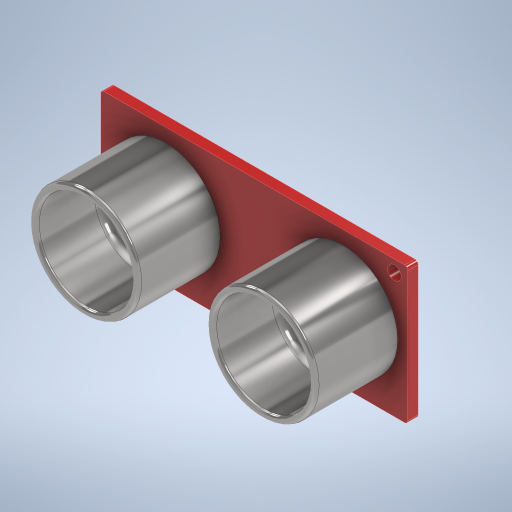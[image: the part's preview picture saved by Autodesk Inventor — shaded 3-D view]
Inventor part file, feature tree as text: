
AUTODESK INVENTOR PART (.ipt)
format: ipt  version: 2023 (Build 270158000, 158)  size: 452,608 bytes
history: native  units: mm
features: extrude x5, fillet x5, other x4, sketch x3, projected_geometry x2, mirror x1
ambient origin geometry x8: Origin, YZ Plane, XZ Plane, XY Plane, X Axis, Y Axis, Z Axis, Center Point
bodies: Body1 (feature_tree), Body2 (feature_tree), Body3 (feature_tree), Body4 (feature_tree)
feature tree (20):
  other  "Sólido1"
  sketch  "Boceto1"  dims[d0=45.0mm d1=20.0mm]
  extrude  "Extrusión1"  Depth=20.0mm
  extrude  "Extrusión2"  Depth=13.0mm
  fillet  "Empalme2"  Radius=13.0mm
  extrude  "Extrusión3"  Depth=0.5mm
  fillet  "Empalme3"  Radius=8.25mm
  fillet  "Empalme4"  Radius=8.25mm
  extrude  "Extrusión4"  Depth=0.5mm
  extrude  "Extrusión5"  Depth=0.5mm TaperAngle=0.0deg
  fillet  "Empalme5"  Radius=1.5mm
  fillet  "Empalme6"  Radius=1.0mm
  mirror  "Simetría1"
  other  "Sólido2"
  sketch  "Boceto2"  dims[d2=16.0mm d3=13.0mm d4=13.0mm]
  projected_geometry  "Contorno proyectado1"
  other  "Sólido3"
  sketch  "Boceto3"  dims[d5=2.0mm d6=20.5mm d7=8.25mm d8=8.25mm d9=20.5mm d10=12.0mm d11=0.0mm d12=1.5mm d13=0.0mm d14=1.0mm d16=0.5mm d17=1.5mm d18=0.0mm d19=2.0mm d20=0.5mm d21=10.5mm d22=2.5mm d23=0.5mm d24=2.5mm d25=0.0mm d26=0.6mm d27=10.5mm d28=1.3125mm d30=2.625mm d31=8.5mm d32=0.0mm d33=0.1mm d34=0.5mm]
  projected_geometry  "Contorno proyectado2"
  other  "Sólido4"
